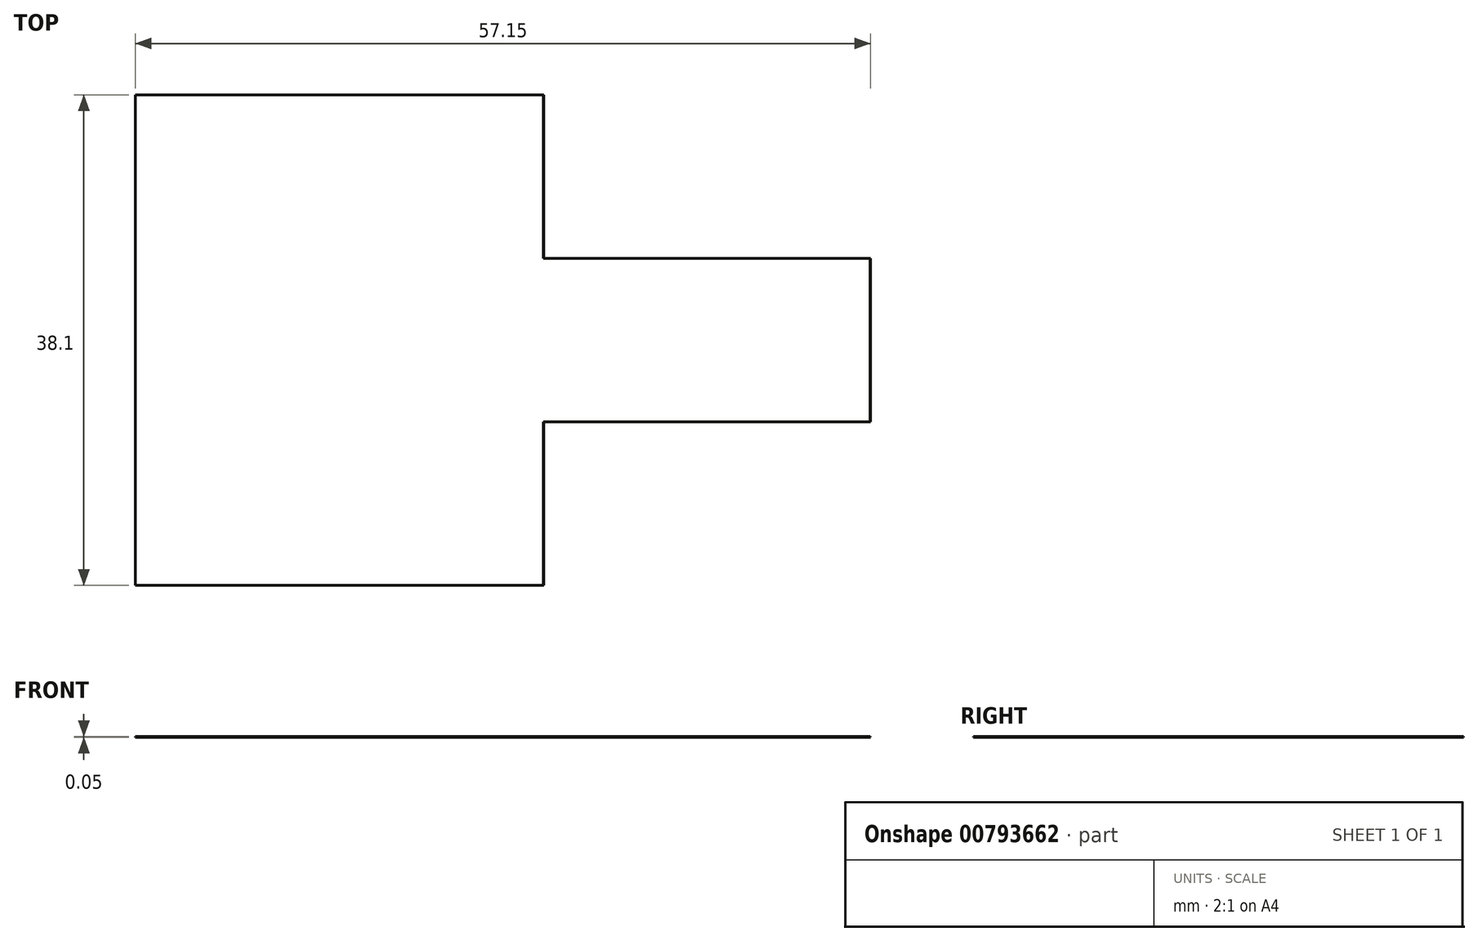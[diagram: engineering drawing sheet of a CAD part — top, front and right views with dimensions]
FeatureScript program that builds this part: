
annotation { "Feature Type Name" : "Feature", "Feature Type Description" : "" }
export const myFeature = defineFeature(function(context is Context, id is Id, definition is map)
    precondition{}
    {
        {
            var Q0;
            Q0=qCreatedBy(makeId("Top.planeOp"),FACE);
            var sketch = newSketch(context, id + "F0", { "sketchPlane" : qUnion([Q0])});
            skLineSegment(sketch, "E0", {"start": v(0, 0) * mm, "end": v(0, -38.1) * mm});
            skLineSegment(sketch, "E1", {"start": v(0, -38.1) * mm, "end": v(31.75, -38.1) * mm});
            skLineSegment(sketch, "E2", {"start": v(31.75, -38.1) * mm, "end": v(31.75, -25.4) * mm});
            skLineSegment(sketch, "E3", {"start": v(31.75, -25.4) * mm, "end": v(57.15, -25.4) * mm});
            skLineSegment(sketch, "E4", {"start": v(57.15, -25.4) * mm, "end": v(57.15, -12.7) * mm});
            skLineSegment(sketch, "E5", {"start": v(57.15, -12.7) * mm, "end": v(31.75, -12.7) * mm});
            skLineSegment(sketch, "E6", {"start": v(31.75, -12.7) * mm, "end": v(31.75, 0) * mm});
            skLineSegment(sketch, "E7", {"start": v(31.75, 0) * mm, "end": v(0, 0) * mm});
            skSolve(sketch);
        }
        {
            var Q0;
            Q0=makeQuery(id+"F0.imprint","IMPRINT",FACE,{"disambiguationData":[TD([[makeQuery(id+"F0.imprint","IMPRINT",EDGE,{"derivedFrom":sQuery(id+"F0.wireOp",EDGE,"E0")}),1.0]])]});
            extrude(context, id + "F1", {"entities" : qUnion([Q0]), "depth" : 5 / 101.6 * mm, "offsetDistance" : 25.4 * mm});
        }
        {
            var Q0;
            Q0=makeQuery(id+"F1.opExtrude","SWEPT_FACE",FACE,{"disambiguationData":[OSD([sQuery(id+"F0.wireOp",EDGE,"E1")])]});
            var sketch = newSketch(context, id + "F2", { "sketchPlane" : qUnion([Q0])});
            skLineSegment(sketch, "E8", {"start": v(31.75, 0) * mm, "end": v(19.05, 31.75) * mm});
            skLineSegment(sketch, "E9", {"start": v(19.05, 31.75) * mm, "end": v(31.75, 31.75) * mm});
            skLineSegment(sketch, "E10", {"start": v(31.75, 31.75) * mm, "end": v(31.75, 0) * mm});
            skSolve(sketch);
        }
        {
            var Q0;
            Q0=makeQuery(id+"F2.imprint","IMPRINT",FACE,{"disambiguationData":[TD([[makeQuery(id+"F2.imprint","IMPRINT",EDGE,{"derivedFrom":sQuery(id+"F2.wireOp",EDGE,"E8")}),-1.0]])]});
            extrude(context, id + "F3", {"entities" : qUnion([Q0]), "operationType" : NewBodyOperationType.REMOVE, "oppositeDirection" : true, "depth" : 12.7 * mm, "offsetDistance" : 25.4 * mm});
        }
        {
            var Q0;
            Q0=makeQuery(id+"F3.boolean.opBoolean","MERGE",FACE,{"derivedFrom":[makeQuery(id+"F1.opExtrude","SWEPT_FACE",FACE,{"disambiguationData":[OSD([sQuery(id+"F0.wireOp",EDGE,"E3")])]}),makeQuery(id+"F3.opExtrude","CAP_FACE",FACE,{"disambiguationData":[OSD([sQuery(id+"F2.wireOp",EDGE,"E8"),sQuery(id+"F2.wireOp",EDGE,"E9"),sQuery(id+"F2.wireOp",EDGE,"E10")])],"isStart":false})]});
            var sketch = newSketch(context, id + "F4", { "sketchPlane" : qUnion([Q0])});
            skLineSegment(sketch, "E11", {"start": v(57.15, 0) * mm, "end": v(57.15, 31.75) * mm});
            skLineSegment(sketch, "E12", {"start": v(57.15, 31.75) * mm, "end": v(44.45, 31.75) * mm});
            skLineSegment(sketch, "E13", {"start": v(44.45, 31.75) * mm, "end": v(57.15, 0) * mm});
            skSolve(sketch);
        }
        {
            var Q0;
            Q0=makeQuery(id+"F4.imprint","IMPRINT",FACE,{"disambiguationData":[TD([[makeQuery(id+"F4.imprint","IMPRINT",EDGE,{"derivedFrom":sQuery(id+"F4.wireOp",EDGE,"E11")}),-1.0]])]});
            extrude(context, id + "F5", {"entities" : qUnion([Q0]), "operationType" : NewBodyOperationType.REMOVE, "oppositeDirection" : true, "depth" : 12.7 * mm, "offsetDistance" : 25.4 * mm});
        }
        {
            var Q0;
            Q0=makeQuery(id+"F1.opExtrude","SWEPT_FACE",FACE,{"disambiguationData":[OSD([sQuery(id+"F0.wireOp",EDGE,"E7")])]});
            var sketch = newSketch(context, id + "F6", { "sketchPlane" : qUnion([Q0])});
            skLineSegment(sketch, "E14", {"start": v(-31.75, 0) * mm, "end": v(-19.05, 31.75) * mm});
            skLineSegment(sketch, "E15", {"start": v(-19.05, 31.75) * mm, "end": v(-31.75, 31.75) * mm});
            skLineSegment(sketch, "E16", {"start": v(-31.75, 31.75) * mm, "end": v(-31.75, 0) * mm});
            skSolve(sketch);
        }
        {
            var Q0;
            Q0=makeQuery(id+"F6.imprint","IMPRINT",FACE,{"disambiguationData":[TD([[makeQuery(id+"F6.imprint","IMPRINT",EDGE,{"derivedFrom":sQuery(id+"F6.wireOp",EDGE,"E14")}),1.0]])]});
            extrude(context, id + "F7", {"entities" : qUnion([Q0]), "operationType" : NewBodyOperationType.REMOVE, "oppositeDirection" : true, "depth" : 12.7 * mm, "offsetDistance" : 25.4 * mm});
        }
    });
